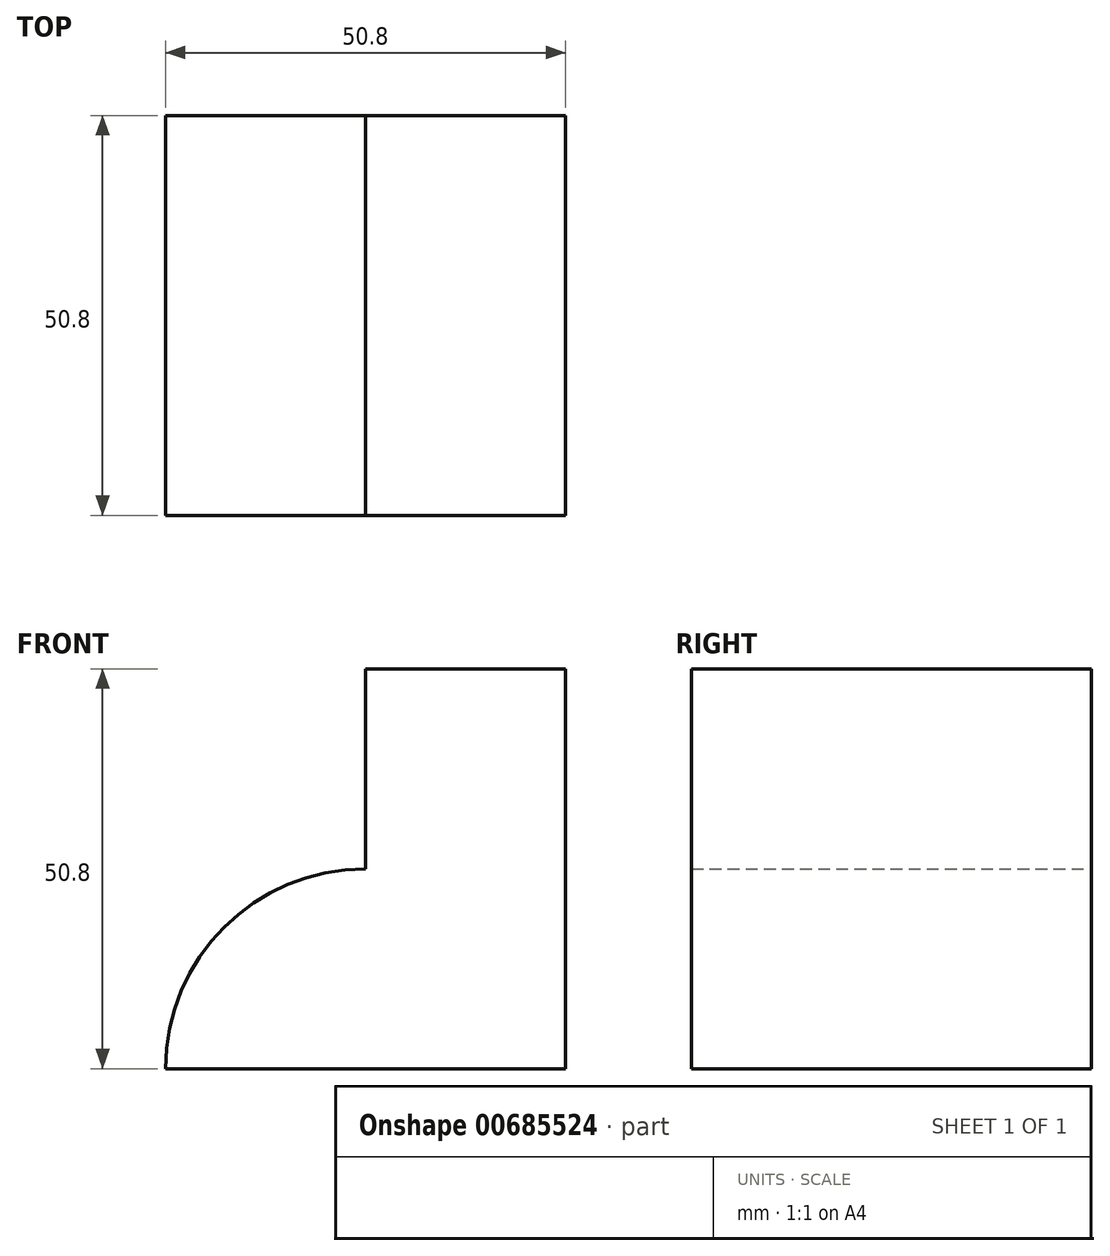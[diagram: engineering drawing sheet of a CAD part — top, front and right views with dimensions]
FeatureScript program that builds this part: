
annotation { "Feature Type Name" : "Feature", "Feature Type Description" : "" }
export const myFeature = defineFeature(function(context is Context, id is Id, definition is map)
    precondition{}
    {
        {
            var Q0;
            Q0=qCreatedBy(makeId("Front.planeOp"),FACE);
            var sketch = newSketch(context, id + "F0", { "sketchPlane" : qUnion([Q0])});
            skLineSegment(sketch, "E0", {"start": v(0, 0) * mm, "end": v(0, -50.8) * mm});
            skLineSegment(sketch, "E1", {"start": v(0, -50.8) * mm, "end": v(-50.8, -50.8) * mm});
            skLineSegment(sketch, "E2", {"start": v(0, 0) * mm, "end": v(-25.4, 0) * mm});
            skLineSegment(sketch, "E3", {"start": v(-25.4, 0) * mm, "end": v(-25.4, -25.4) * mm});
            skArc(sketch, "E4", {"start": v(-25.4, -25.4) * mm, "mid": v(-43.36, -32.84) * mm, "end": v(-50.8, -50.8) * mm});
            skSolve(sketch);
        }
        {
            var Q0;
            Q0=makeQuery(id+"F0.imprint","IMPRINT",FACE,{"disambiguationData":[TD([[makeQuery(id+"F0.imprint","IMPRINT",EDGE,{"derivedFrom":sQuery(id+"F0.wireOp",EDGE,"E0")}),-1.0]])]});
            extrude(context, id + "F1", {"entities" : qUnion([Q0]), "depth" : 50.8 * mm, "offsetDistance" : 25.4 * mm});
        }
    });
